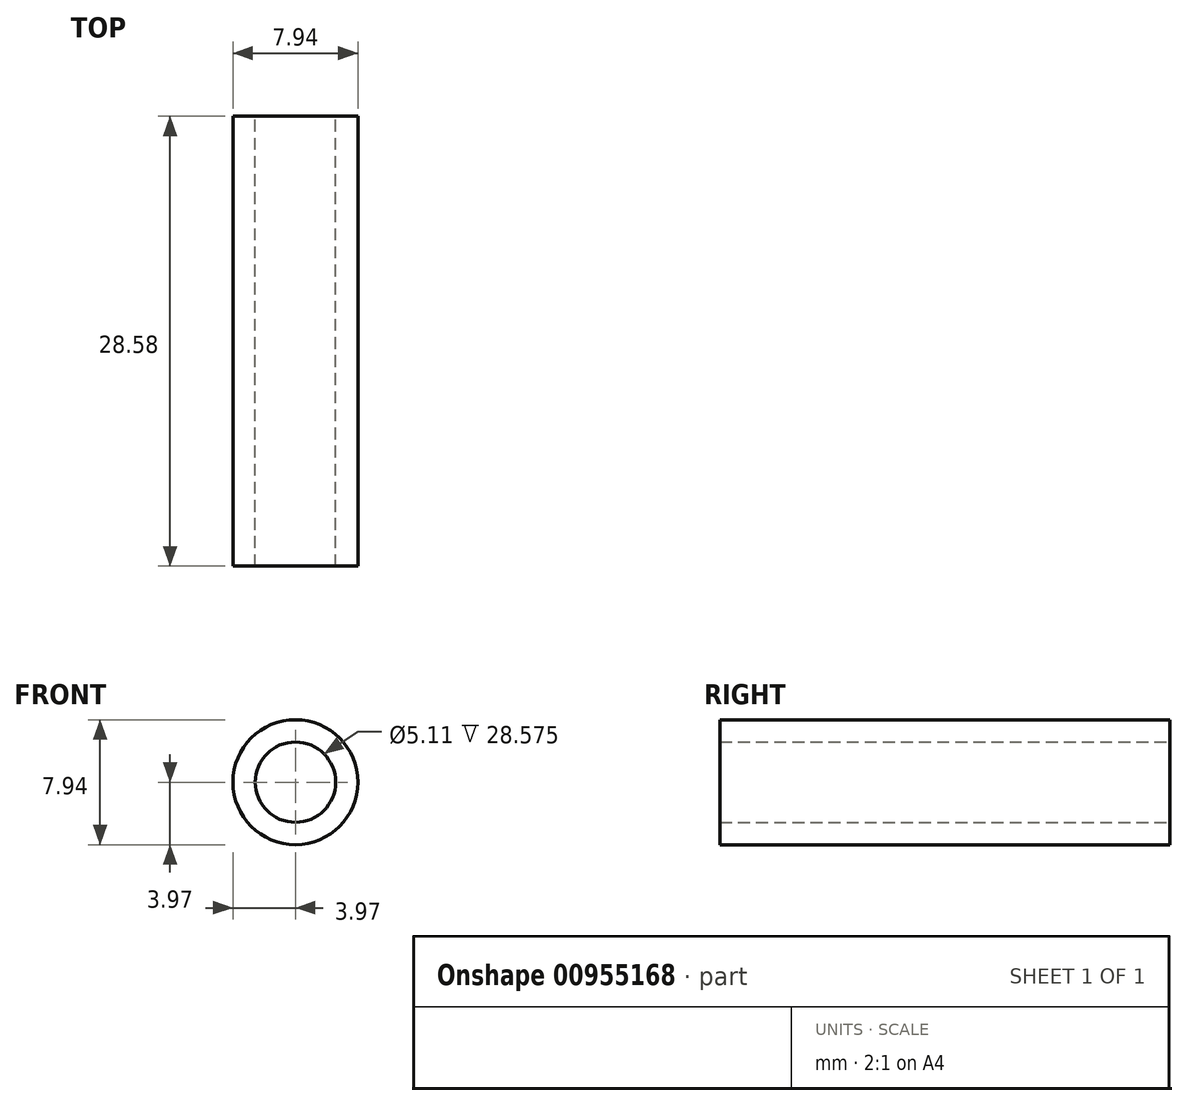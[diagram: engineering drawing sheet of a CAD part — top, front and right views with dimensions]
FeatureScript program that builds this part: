
annotation { "Feature Type Name" : "Feature", "Feature Type Description" : "" }
export const myFeature = defineFeature(function(context is Context, id is Id, definition is map)
    precondition{}
    {
        {
            var Q0;
            Q0=qCreatedBy(makeId("Front.planeOp"),FACE);
            var sketch = newSketch(context, id + "F0", { "sketchPlane" : qUnion([Q0])});
            skCircle(sketch, "E0", {"center": v(0, 0) * mm, "radius": 3.97 * mm});
            skCircle(sketch, "E1", {"center": v(0, 0) * mm, "radius": 2.55 * mm});
            skSolve(sketch);
        }
        {
            var Q0;
            Q0=qSketchRegion(id+"F0",true);
            extrude(context, id + "F1", {"entities" : qUnion([Q0]), "depth" : 28.57 * mm, "offsetDistance" : 25.4 * mm});
        }
    });
